# Revit family: NBS_GreshamOfficeFurnitureLtd_OffcChrs_UnoaBooth
name_source: partatom
category: Furniture
units: mm (PartAtom-declared; Revit-internal decimal feet)

## family parameters
Always vertical = Yes
Cut with Voids When Loaded = No
Room Calculation Point = No
Shared = No
Work Plane-Based = No

## types (2) — shared parameters
Adjustability = Non-adjustable
AssetType = Movable
Base = Beech wood,Painted,Raw
BoothFrameMaterial = NBS_GreshamOfficeFurniture_Wood
Category = Pr_40_50_12_57:Office chairs
Color = Other
Description = Reception, breakout and soft booth office seating
DurationUnit = year
FabricMaterial = NBS_GreshamOfficeFurniture_Grey
Features = Comfortable, private, choice of fabrics, non-removable seat cushions, choice of frame styles and finishes
Finish = Other,Painted
FrameMaterial = Tubular metal
HalfBooth = Yes
Height = 430 mm  [stored 1.41076 ft]
IfcExportAs = IfcFurnitureType
IfcExportType = USERDEFINED
ManufacturerName = Gresham Office Furniture Ltd
ManufacturerURL = www.gof.co.uk
Material = Metal,Polyurethane,Wood,Fabric
ModelNumber = UNOBA1, UNOBA2
ModelReference = Unoa Booth
NBSInstanceId = 8ba6d46b-b5bb-459e-abf4-220fa4e06cd6
NBSObjectId = 8f5481b6-722a-4462-9116-943a82b467d3
NominalHeight = 1310 mm  [stored 4.2979 ft]
OverallHeight = 1310 mm  [stored 4.2979 ft]
ProductInformation = https://source.thenbs.com
SeatsAndBacksFinish = Upholstered
SeatsAndBacksMaterial = Cold foamed polyurethane
Shape = Rectangle,Other
StandardsDurability = To BS EN 16139
TableFrameMaterial = NBS_GreshamOfficeFurniture_Black
Uniclass2015Code = Pr_40_50_12_57
Uniclass2015Title = Office chairs
Uniclass2015Version = Products v1.29
Version = 2
WarrantyDescription = Five year
WarrantyDurationParts = Five year guarantee
WarrantyDurationUnit = year
zero-valued in all types: Default Elevation

## per-type parameters (varying)
| type | BIMObjectName | Constituents | FullBoothWithTable | NBSVariantId | Name | NominalLength | NominalWidth | OverallDepth | OverallWidth | Size |
| UNOBA1HalfBoothWithoutTable | NBS_GreshamOfficeFurnitureLtd_OfficeChairs_UnoaBooth_UNOBA1HalfBoothWithoutTable | Half booth | No | 26dee803-ecf8-a498-737c-a90f1c510233 | OfficeChairs_UnoaBooth_UNOBA1HalfBoothWithoutTable_GreshamOfficeFurnitureLtd | 700 mm  [stored 2.29659 ft] | 1390 mm  [stored 4.56037 ft] | 700 mm  [stored 2.29659 ft] | 1390 mm  [stored 4.56037 ft] | 1310 x 1390 x 700 mm |
| UNOBA2FullBoothWithTable | NBS_GreshamOfficeFurnitureLtd_OfficeChairs_UnoaBooth_UNOBA2FullBoothWithTable | Full booth with table | Yes | f0b4f5c3-34b2-4e86-33b8-f22a8563207d | OfficeChairs_UnoaBooth_UNOBA2FullBoothWithTable_GreshamOfficeFurnitureLtd | 1390 mm  [stored 4.56037 ft] | 2380 mm  [stored 7.8084 ft] | 1390 mm  [stored 4.56037 ft] | 2380 mm  [stored 7.8084 ft] | 1310 x 2380 x 1390 mm |

note: [stored X ft] marks values corroborated as IEEE doubles in the binary element streams (Revit-internal decimal feet)

## geometry (parser evidence)
native form markers: Sweep x2
no freeform markers — native parametric forms only
